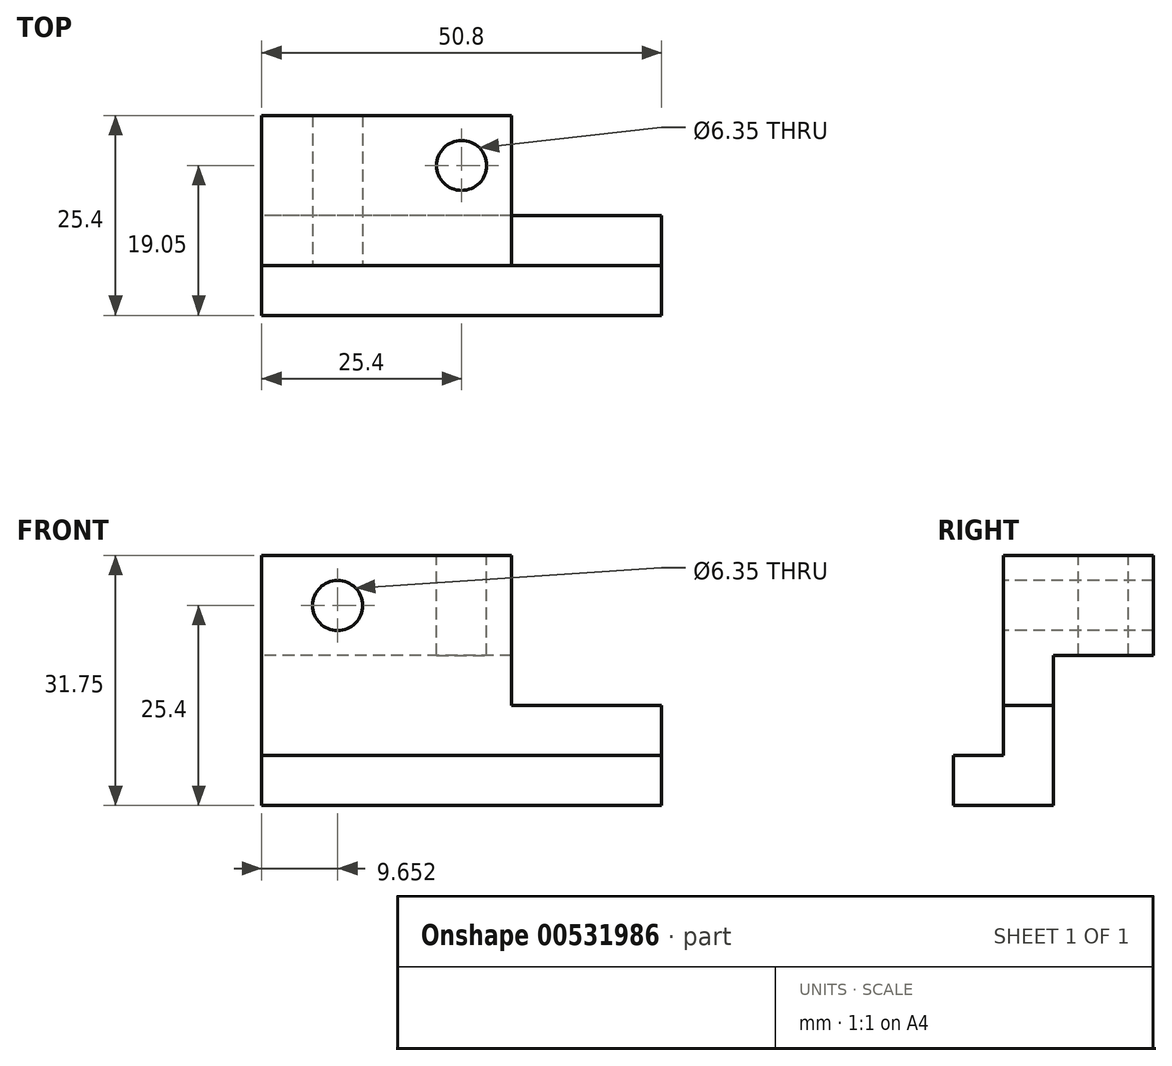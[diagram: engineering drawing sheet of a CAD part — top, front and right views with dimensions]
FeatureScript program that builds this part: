
annotation { "Feature Type Name" : "Feature", "Feature Type Description" : "" }
export const myFeature = defineFeature(function(context is Context, id is Id, definition is map)
    precondition{}
    {
        {
            var Q0;
            Q0=qCreatedBy(makeId("Right.planeOp"),FACE);
            var sketch = newSketch(context, id + "F0", { "sketchPlane" : qUnion([Q0])});
            skLineSegment(sketch, "E0.bottom", {"start": v(0, 0) * mm, "end": v(-19.05, 0) * mm});
            skLineSegment(sketch, "E0.top", {"start": v(0, -12.7) * mm, "end": v(-19.05, -12.7) * mm});
            skLineSegment(sketch, "E0.left", {"start": v(0, 0) * mm, "end": v(0, -12.7) * mm});
            skLineSegment(sketch, "E0.right", {"start": v(-19.05, 0) * mm, "end": v(-19.05, -12.7) * mm});
            skSolve(sketch);
        }
        {
            var Q0;
            Q0 = qSketchRegion(id + "F0", true);
            extrude(context, id + "F1", {"entities" : qUnion([Q0]), "depth" : 31.75 * mm, "offsetDistance" : 25.4 * mm});
        }
        {
            var Q0;
            Q0=makeQuery(id+"F1.opExtrude","CAP_FACE",FACE,{"disambiguationData":[OSD([sQuery(id+"F0.wireOp",EDGE,"E0.bottom"),sQuery(id+"F0.wireOp",EDGE,"E0.top"),sQuery(id+"F0.wireOp",EDGE,"E0.left"),sQuery(id+"F0.wireOp",EDGE,"E0.right")])],"isStart":true});
            var sketch = newSketch(context, id + "F2", { "sketchPlane" : qUnion([Q0])});
            skLineSegment(sketch, "E1.bottom", {"start": v(19.05, -12.7) * mm, "end": v(12.7, -12.7) * mm});
            skLineSegment(sketch, "E1.top", {"start": v(19.05, -19.05) * mm, "end": v(12.7, -19.05) * mm});
            skLineSegment(sketch, "E1.left", {"start": v(19.05, -12.7) * mm, "end": v(19.05, -19.05) * mm});
            skLineSegment(sketch, "E1.right", {"start": v(12.7, -12.7) * mm, "end": v(12.7, -19.05) * mm});
            skSolve(sketch);
        }
        {
            var Q0;
            Q0 = qSketchRegion(id + "F2", true);
            extrude(context, id + "F3", {"entities" : qUnion([Q0]), "operationType" : NewBodyOperationType.ADD, "oppositeDirection" : true, "depth" : 31.75 * mm, "offsetDistance" : 25.4 * mm});
        }
        {
            var Q0;
            Q0=makeQuery(id+"F3.boolean.opBoolean","MERGE",FACE,{"derivedFrom":[makeQuery(id+"F1.opExtrude","CAP_FACE",FACE,{"disambiguationData":[OSD([sQuery(id+"F0.wireOp",EDGE,"E0.bottom"),sQuery(id+"F0.wireOp",EDGE,"E0.top"),sQuery(id+"F0.wireOp",EDGE,"E0.left"),sQuery(id+"F0.wireOp",EDGE,"E0.right")])],"isStart":true}),makeQuery(id+"F3.opExtrude","CAP_FACE",FACE,{"disambiguationData":[OSD([sQuery(id+"F2.wireOp",EDGE,"E1.bottom"),sQuery(id+"F2.wireOp",EDGE,"E1.top"),sQuery(id+"F2.wireOp",EDGE,"E1.left"),sQuery(id+"F2.wireOp",EDGE,"E1.right")])],"isStart":true})]});
            var sketch = newSketch(context, id + "F4", { "sketchPlane" : qUnion([Q0])});
            skLineSegment(sketch, "E2", {"start": v(19.05, -19.05) * mm, "end": v(19.05, -25.4) * mm});
            skLineSegment(sketch, "E3", {"start": v(19.05, -25.4) * mm, "end": v(25.4, -25.4) * mm});
            skLineSegment(sketch, "E4", {"start": v(25.4, -25.4) * mm, "end": v(25.4, -31.75) * mm});
            skLineSegment(sketch, "E5", {"start": v(25.4, -31.75) * mm, "end": v(12.7, -31.75) * mm});
            skLineSegment(sketch, "E6", {"start": v(12.7, -31.75) * mm, "end": v(12.7, -19.05) * mm});
            skLineSegment(sketch, "E7", {"start": v(19.05, -19.05) * mm, "end": v(12.7, -19.05) * mm});
            skSolve(sketch);
        }
        {
            var Q0;
            Q0 = qSketchRegion(id + "F4", true);
            extrude(context, id + "F5", {"entities" : qUnion([Q0]), "operationType" : NewBodyOperationType.ADD, "oppositeDirection" : true, "depth" : 50.8 * mm, "offsetDistance" : 25.4 * mm});
        }
        {
            var Q0;
            Q0=makeQuery(id+"F1.opExtrude","SWEPT_FACE",FACE,{"disambiguationData":[OSD([sQuery(id+"F0.wireOp",EDGE,"E0.bottom")])]});
            var sketch = newSketch(context, id + "F6", { "sketchPlane" : qUnion([Q0])});
            skCircle(sketch, "E8", {"center": v(25.4, -6.35) * mm, "radius": 3.18 * mm});
            skSolve(sketch);
        }
        {
            var Q0;
            Q0 = qSketchRegion(id + "F6", true);
            extrude(context, id + "F7", {"entities" : qUnion([Q0]), "operationType" : NewBodyOperationType.REMOVE, "endBound" : BoundingType.THROUGH_ALL, "oppositeDirection" : true, "depth" : 25.4 * mm, "offsetDistance" : 25.4 * mm});
        }
        {
            var Q0;
            Q0=makeQuery(id+"F5.boolean.opBoolean","MERGE",FACE,{"derivedFrom":[makeQuery(id+"F3.boolean.opBoolean","MERGE",FACE,{"derivedFrom":[makeQuery(id+"F1.opExtrude","SWEPT_FACE",FACE,{"disambiguationData":[OSD([sQuery(id+"F0.wireOp",EDGE,"E0.right")])]}),makeQuery(id+"F3.opExtrude","SWEPT_FACE",FACE,{"disambiguationData":[OSD([sQuery(id+"F2.wireOp",EDGE,"E1.left")])]})]}),makeQuery(id+"F5.opExtrude","SWEPT_FACE",FACE,{"disambiguationData":[OSD([sQuery(id+"F4.wireOp",EDGE,"E2")])]})]});
            var sketch = newSketch(context, id + "F8", { "sketchPlane" : qUnion([Q0])});
            skCircle(sketch, "E9", {"center": v(9.65, -6.35) * mm, "radius": 3.18 * mm});
            skSolve(sketch);
        }
        {
            var Q0;
            Q0 = qSketchRegion(id + "F8", true);
            extrude(context, id + "F9", {"entities" : qUnion([Q0]), "operationType" : NewBodyOperationType.REMOVE, "endBound" : BoundingType.THROUGH_ALL, "oppositeDirection" : true, "depth" : 25.4 * mm, "offsetDistance" : 25.4 * mm});
        }
    });
